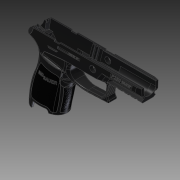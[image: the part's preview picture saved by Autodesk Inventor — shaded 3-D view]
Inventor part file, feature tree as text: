
AUTODESK INVENTOR PART (.ipt)
format: ipt  version: 2014 SP2 (Build 180246200, 246)  size: 58,253,824 bytes
history: native  units: in
note: dims shown in document units (in); Inventor stores cm internally (conversion verified against a paired STEP export)
features: sketch x143, projected_geometry x76, extrude x69, plane x53, reference x51, fillet x25, other x19, sweep x17, loft x7, delete_face x6, mirror x5, boolean_combine x5, surface_op x5, split x3, emboss x3, move_body x2, imported_body x1, chamfer x1, pattern_linear x1, revolve x1
ambient origin geometry x8: Origin, YZ Plane, XZ Plane, XY Plane, X Axis, Y Axis, Z Axis, Center Point
bodies: Solid6 (feature_tree), Solid9 (feature_tree), Solid23 (feature_tree), Solid7 (feature_tree), Solid8 (feature_tree), Solid10 (feature_tree), Solid21 (feature_tree), Solid22 (feature_tree)
feature tree (493):
  sketch  "Sketch1"  dims[d1=4.4533in d14=75.0deg]
  sketch  "Sketch2"  dims[d15=0.8575in d16=15.0deg]
  plane  "Work Plane1"
  plane  "Work Plane2"
  plane  "Work Plane6"
  plane  "Work Plane21"
  sketch  "Sketch12"  dims[d17=0.045in d18=4.1515in]
  plane  "Work Plane22"
  plane  "Work Plane29"
  sketch  "Sketch47"  dims[d19=90.0deg d20=90.0deg d21=0.5625in]
  sketch  "Sketch48"  dims[d22=0.5in d23=0.638in]
  plane  "Work Plane30"
  sketch  "Sketch49"  dims[d24=2.26in d25=0.6031in]
  plane  "Work Plane32"
  plane  "Work Plane31"
  loft  "Loft14"
  extrude  "Extrusion11"  TaperAngle=15.0deg  [1 undecoded]
  mirror  "Mirror2"
  sweep  "Sweep13"
  sketch  "Sketch65"  dims[d189=1.313in d190=0.5625in]
  sketch  "Sketch66"  dims[d191=0.0in d218=0.0in d219=90.0deg]
  sketch  "Sketch67"  dims[d220=0.0in d221=90.0deg d222=0.0in d223=90.0deg]
  sketch  "Sketch68"  dims[d224=0.0in d225=90.0deg d227=1.0in d228=0.0in]
  plane  "Work Plane34"
  loft  "Loft16"
  mirror  "Mirror4"
  sweep  "Sweep15"
  mirror  "Mirror5"
  sketch  "Sketch72"  dims[d255=0.0in d256=90.0deg d257=1.4375in]
  sketch  "Sketch73"  dims[d258=0.0in d264=0.149in]
  sketch  "Sketch74"  dims[d267=0.507in d268=1.2in]
  plane  "Work Plane35"
  sketch  "Sketch75"  dims[d275=0.7171in d276=0.0in d298=2.7754in d310=0.5065in]
  extrude  "Extrusion16"  Depth=0.6031in
  split  "Split1"
  boolean_combine  "Combine1"
  sketch  "Sketch104"  dims[d313=2.4322in d314=0.0in d315=90.0deg]
  sketch  "Sketch105"  dims[d316=0.0in d317=90.0deg d318=0.0in d319=90.0deg]
  loft  "Loft19"
  delete_face  "Delete Face1"
  delete_face  "Delete Face2"
  delete_face  "Delete Face3"
  delete_face  "Delete Face4"
  plane  "Work Plane37"
  plane  "Work Plane38"
  plane  "Work Plane39"
  plane  "Work Plane40"
  boolean_combine  "Combine3"
  fillet  "Fillet14"  Radius=0.3232in
  plane  "Work Plane41"
  extrude  "Extrusion18"  TaperAngle=0.0deg  [1 undecoded]
  sketch  "Sketch116"  dims[d363=0.005in d364=1.0in d365=0.0in]
  plane  "Work Plane42"
  extrude  "Extrusion19"  Depth=0.5625in
  extrude  "Extrusion20"  TaperAngle=0.0deg  [1 undecoded]
  sketch  "Sketch119"  dims[d371=0.005in d372=1.0in d373=0.0in]
  plane  "Work Plane43"
  plane  "Work Plane44"
  extrude  "Extrusion21"  TaperAngle=0.0deg  [1 undecoded]
  sweep  "Sweep20"
  extrude  "Extrusion22"  TaperAngle=0.0deg  [1 undecoded]
  plane  "Work Plane45"
  extrude  "Extrusion23"  TaperAngle=0.0deg  [1 undecoded]
  extrude  "Extrusion24"  TaperAngle=0.0deg  [1 undecoded]
  extrude  "Extrusion25"  Depth=1.4375in
  plane  "Work Plane46"
  sweep  "Sweep21"
  extrude  "Extrusion26"  Depth=1.2in
  extrude  "Extrusion27"  Depth=2.7754in
  fillet  "Fillet18"  Radius=0.5065in
  imported_body  "Base1"
  move_body  "Move Body1"
  extrude  "Extrusion28"  Depth=2.4322in
  move_body  "Move Body2"
  extrude  "Extrusion29"  TaperAngle=0.0deg  [1 undecoded]
  extrude  "Extrusion30"  TaperAngle=0.0deg  [1 undecoded]
  extrude  "Extrusion33"  Depth=0.005in
  extrude  "Extrusion34"  Depth=1.0in TaperAngle=0.0deg
  sketch  "Sketch138"  dims[d412=0.303in]
  extrude  "Extrusion35"  TaperAngle=90.0deg  [1 undecoded]
  extrude  "Extrusion36"  Depth=1.0in TaperAngle=0.0deg
  sweep  "Sweep23"
  extrude  "Extrusion37"  Depth=0.005in
  chamfer  "Chamfer1"  Distance=1.0in
  plane  "Work Plane51"
  extrude  "Extrusion44"  Depth=0.762in
  sketch  "Sketch144"  dims[d417=0.05in d418=0.0in d419=0.0in]
  plane  "Work Plane53"
  extrude  "Extrusion45"  Depth=0.6475in
  plane  "Work Plane54"
  extrude  "Extrusion46"  Depth=1.567in
  plane  "Work Plane55"
  extrude  "Extrusion47"  Depth=0.01in
  sweep  "Sweep26"
  sweep  "Sweep27"
  plane  "Work Plane56"
  extrude  "Extrusion52"  Depth=0.1945in
  fillet  "Fillet19"  Radius=3.5375in
  extrude  "Extrusion53"  Depth=3.5375in TaperAngle=0.0deg
  extrude  "Extrusion54"  TaperAngle=0.0deg  [1 undecoded]
  pattern_linear  "Rectangular Pattern1"  Count1=4 Spacing1=0.3937in
  sketch  "Sketch166"  dims[d445=0.138in]
  extrude  "Extrusion55"  Depth=1.2795in
  extrude  "Extrusion56"  Depth=0.0098in TaperAngle=0.0deg
  sketch  "Sketch167"  dims[d446=0.2135in]
  plane  "Work Plane57"
  sketch  "Sketch168"  dims[d447=0.679in]
  plane  "Work Plane58"
  extrude  "Extrusion57"  Depth=0.4764in
  extrude  "Extrusion58"  Depth=0.5602in
  extrude  "Extrusion59"  Depth=0.0134in TaperAngle=0.0deg
  sweep  "Sweep28"
  plane  "Work Plane59"
  extrude  "Extrusion60"  Depth=0.0134in TaperAngle=0.0deg
  sketch  "Sketch174"  dims[d457=0.013in d458=0.0in]
  sketch  "Sketch175"  dims[d459=0.0in]
  extrude  "Extrusion61"  [1 undecoded]
  extrude  "Extrusion62"  Depth=0.2295in
  extrude  "Extrusion63"  Depth=0.089in
  plane  "Work Plane73"
  sweep  "Sweep29"
  plane  "Work Plane60"
  extrude  "Extrusion64"  Depth=3.0134in TaperAngle=0.0deg
  fillet  "Fillet21"  Radius=0.0787in
  extrude  "Extrusion65"  TaperAngle=0.0deg  [1 undecoded]
  extrude  "Extrusion66"  Depth=0.1969in
  sweep  "Sweep30"
  fillet  "Fillet22"  Radius=0.3884in
  fillet  "Fillet23"  Radius=0.05in
  sketch  "Sketch186"  dims[d477=0.1079in]
  extrude  "Extrusion70"  Depth=0.01in TaperAngle=0.0deg
  fillet  "Fillet24"  [1 undecoded]
  other  "OUTLINE"
  plane  "Work Plane62"
  sketch  "Sketch197"  dims[d488=0.8325in]
  extrude  "Extrusion72"  Depth=0.025in
  boolean_combine  "Combine4"
  extrude  "Extrusion73"  Depth=0.09in
  extrude  "Extrusion74"  Depth=0.075in
  extrude  "Extrusion75"  Depth=0.8765in TaperAngle=0.0deg
  extrude  "Extrusion76"  Depth=0.8765in TaperAngle=0.0deg
  fillet  "Fillet27"  Radius=0.8765in
  extrude  "Extrusion77"  Depth=0.15in
  sketch  "Sketch219"  dims[d512=0.3779in]
  plane  "Work Plane65"
  extrude  "Extrusion78"  TaperAngle=0.0deg  [1 undecoded]
  plane  "Work Plane66"
  plane  "Work Plane70"
  sketch  "Sketch226"  dims[d513=0.2425in]
  plane  "Work Plane71"
  extrude  "Extrusion80"  Depth=0.125in
  sweep  "Sweep33"
  plane  "Work Plane72"
  sketch  "Sketch233"  dims[d518=0.0in]
  sketch  "Sketch234"  dims[d527=0.125in]
  split  "Split7"
  loft  "Loft27"
  boolean_combine  "Combine5"
  extrude  "Extrusion84"  Depth=1.0321in
  sketch  "Sketch237"  dims[d531=0.2106in]
  sketch  "Sketch238"  dims[d532=0.1685in]
  sweep  "Sweep34"
  plane  "Work Plane75"
  surface_op  "Trim1"
  surface_op  "Trim2"
  sketch  "Sketch261"  dims[d543=0.4945in d544=0.0098in d545=0.0in]
  surface_op  "Stitch Surface2"
  boolean_combine  "Combine6"
  plane  "Work Plane76"
  sketch  "Sketch262"  dims[d546=0.0098in d547=0.0in d548=0.4764in]
  plane  "Work Plane77"
  extrude  "Extrusion90"  Depth=0.5822in
  fillet  "Fillet41"  Radius=2.1701in
  revolve  "Revolution1"  [1 undecoded]
  plane  "Work Plane78"
  extrude  "Extrusion91"  TaperAngle=0.0deg  [1 undecoded]
  split  "Split8"
  delete_face  "Delete Face7"
  surface_op  "Stitch Surface3"
  plane  "Work Plane79"
  plane  "Work Plane80"
  extrude  "Extrusion92"  Depth=1.0in TaperAngle=0.0deg
  delete_face  "Delete Face9"
  fillet  "Fillet48"  [1 undecoded]
  fillet  "Fillet49"  [1 undecoded]
  fillet  "Fillet50"  [1 undecoded]
  fillet  "Fillet51"  Radius=0.375in
  fillet  "Fillet52"  Radius=0.375in
  fillet  "Fillet53"  [1 undecoded]
  fillet  "Fillet54"  [1 undecoded]
  fillet  "Fillet55"  [1 undecoded]
  extrude  "Extrusion93"  TaperAngle=0.0deg  [1 undecoded]
  extrude  "Extrusion94"  TaperAngle=0.0deg  [1 undecoded]
  fillet  "Fillet58"  [1 undecoded]
  fillet  "Fillet59"  Radius=1.0in
  extrude  "Extrusion95"  Depth=0.0137in
  extrude  "Extrusion96"  [1 undecoded]
  extrude  "Extrusion97"  Depth=0.25in TaperAngle=0.0deg
  sweep  "Sweep35"
  extrude  "Extrusion98"  Depth=0.1969in
  mirror  "Mirror12"
  extrude  "Extrusion99"  Depth=0.1969in
  extrude  "Extrusion100"  Depth=0.1969in
  extrude  "Extrusion101"  Depth=0.1969in
  extrude  "Extrusion102"  Depth=0.1969in
  extrude  "Extrusion103"  Depth=0.1969in
  fillet  "Fillet60"  Radius=0.1969in
  sweep  "Sweep36"
  sketch  "Sketch298"  dims[d643=1.0in d644=0.0in d645=0.0in]
  plane  "Work Plane83"
  extrude  "Extrusion104"  Depth=0.1969in
  sketch  "Sketch299"  dims[d646=1.0in d647=0.0in d648=0.125in]
  plane  "Work Plane84"
  extrude  "Extrusion105"  TaperAngle=0.0deg  [1 undecoded]
  fillet  "Fillet61"  [1 undecoded]
  fillet  "Fillet62"  Radius=1.0in
  fillet  "Fillet63"  Radius=0.0369in
  fillet  "Fillet64"  Radius=0.4in
  plane  "Work Plane85"
  sketch  "Sketch300"  dims[d671=0.765in d672=90.0deg]
  sketch  "3D Sketch50"
  plane  "Work Plane86"
  sweep  "Sweep37"
  mirror  "Mirror13"
  plane  "Work Plane87"
  sketch  "Sketch302"  dims[d682=90.0deg d683=1.0321in]
  sketch  "3D Sketch51"
  plane  "Work Plane88"
  sweep  "Sweep38"
  plane  "Work Plane89"
  sketch  "Sketch305"  dims[d686=2.1701in d688=0.5822in d689=2.1701in]
  sketch  "3D Sketch52"
  plane  "Work Plane90"
  sweep  "Sweep40"
  plane  "Work Plane91"
  emboss  "Emboss2"
  plane  "Work Plane92"
  emboss  "Emboss3"
  extrude  "Extrusion106"  Depth=1.5in
  other  "Move Face2"
  emboss  "Emboss4"
  extrude  "Extrusion107"  Depth=0.04in
  fillet  "Fillet65"  Radius=0.02in
  other  "Image1"
  reference  "Reference1"
  reference  "Reference2"
  reference  "Reference3"
  reference  "Reference4"
  reference  "Reference5"
  reference  "Reference6"
  reference  "Reference7"
  reference  "Reference8"
  reference  "Reference9"
  reference  "Reference10"
  sketch  "Sketch62"  dims[d51=1.056in d53=0.6395in d55=0.3232in]
  projected_geometry  "Projected Loop23"
  sketch  "Sketch63"  dims[d56=0.3593in d187=0.0in]
  projected_geometry  "Projected Loop25"
  projected_geometry  "Projected Loop26"
  sketch  "Sketch69"  dims[d243=0.5822in d245=0.0in]
  other  "Edges3"
  sketch  "Sketch70"  dims[d247=0.0in d248=90.0deg d249=0.0in d250=90.0deg]
  projected_geometry  "Projected Loop27"
  sketch  "Sketch71"  dims[d251=0.0in d252=90.0deg d253=0.0in d254=90.0deg]
  sketch  "Sketch101"  dims[d311=0.5065in d312=2.4322in]
  projected_geometry  "Projected Loop34"
  sketch  "3D Sketch23"
  sketch  "Sketch115"  dims[d336=0.3125in d362=0.005in]
  reference  "Reference11"
  reference  "Reference12"
  reference  "Reference13"
  reference  "Reference14"
  reference  "Reference15"
  reference  "Reference16"
  reference  "Reference17"
  reference  "Reference18"
  reference  "Reference19"
  sketch  "Sketch117"  dims[d366=0.01in d367=90.0deg]
  reference  "Reference20"
  reference  "Reference21"
  sketch  "Sketch118"  dims[d368=0.01in d369=1.0in d370=0.0in]
  reference  "Reference22"
  reference  "Reference23"
  reference  "Reference24"
  reference  "Reference25"
  reference  "Reference26"
  reference  "Reference27"
  reference  "Reference28"
  reference  "Reference29"
  reference  "Reference30"
  reference  "Reference31"
  sketch  "Sketch120"  dims[d374=0.01in d375=0.005in]
  projected_geometry  "Projected Loop37"
  sketch  "Sketch121"  dims[d378=0.01in]
  projected_geometry  "Projected Loop38"
  sketch  "3D Sketch27"
  sketch  "Sketch122"  dims[d379=-0.0745in]
  projected_geometry  "Projected Loop39"
  projected_geometry  "Projected Loop40"
  reference  "Reference32"
  reference  "Reference33"
  reference  "Reference34"
  reference  "Reference35"
  reference  "Reference36"
  sketch  "Sketch123"  dims[d380=0.025in]
  reference  "Reference37"
  sketch  "Sketch125"  dims[d381=0.2188in d382=1.0in d383=0.0in]
  projected_geometry  "Projected Loop42"
  sketch  "Sketch126"  dims[d384=0.0in d385=0.762in]
  reference  "Reference38"
  sketch  "Sketch127"  dims[d386=0.1455in d388=0.6475in]
  sketch  "Sketch128"  dims[d389=0.01in d390=1.567in]
  sketch  "Sketch129"  dims[d391=0.68in d392=0.01in]
  sketch  "Sketch130"  dims[d393=0.01in d394=1.0in d395=0.0in]
  projected_geometry  "Projected Loop43"
  sketch  "Sketch131"  dims[d396=0.19in d397=0.01in]
  sketch  "Sketch132"  dims[d398=0.085in d399=0.0in d400=0.1945in d401=3.5375in d402=0.0in]
  reference  "Reference39"
  sketch  "Sketch133"  dims[d403=0.344in d404=3.5375in d405=0.0in]
  projected_geometry  "Projected Loop44"
  sketch  "Sketch136"  dims[d407=-0.286in d409=0.0in]
  reference  "Reference40"
  sketch  "Sketch137"  dims[d410=0.0in d411=0.0in]
  projected_geometry  "Projected Loop45"
  projected_geometry  "Projected Loop46"
  sketch  "Sketch139"  dims[d413=0.0785in]
  projected_geometry  "Projected Loop47"
  sketch  "Sketch140"  dims[d414=3.5375in d415=0.0in]
  projected_geometry  "Projected Loop48"
  sketch  "3D Sketch29"
  sketch  "Sketch141"  dims[d416=0.4in]
  projected_geometry  "Projected Loop49"
  projected_geometry  "Projected Loop52"
  sketch  "Sketch153"  dims[d421=0.3575in]
  projected_geometry  "Projected Loop58"
  sketch  "Sketch154"  dims[d422=3.5375in d423=0.0in]
  sketch  "Sketch155"  dims[d424=0.2645in]
  projected_geometry  "Projected Loop59"
  sketch  "Sketch156"  dims[d425=45.0deg]
  sketch  "Sketch157"  dims[d426=0.0in d427=0.015in d428=0.0in d429=0.02in]
  projected_geometry  "Projected Loop60"
  sketch  "Sketch158"  dims[d430=0.092in]
  projected_geometry  "Projected Loop61"
  sketch  "Sketch160"  dims[d431=0.6in]
  sketch  "Sketch164"  dims[d432=0.062in d433=0.0in]
  projected_geometry  "Projected Loop63"
  projected_geometry  "Projected Loop64"
  sketch  "Sketch165"  dims[d434=0.062in d435=0.0in]
  projected_geometry  "Projected Loop65"
  projected_geometry  "Projected Loop66"
  projected_geometry  "Projected Loop67"
  sketch  "Sketch169"  dims[d448=0.187in d449=0.0in]
  sketch  "Sketch170"  dims[d450=0.7in]
  projected_geometry  "Projected Loop68"
  sketch  "Sketch171"  dims[d451=0.013in d452=0.0in]
  projected_geometry  "Projected Loop69"
  sketch  "Sketch172"  dims[d454=0.6385in]
  projected_geometry  "Projected Loop70"
  projected_geometry  "Projected Loop71"
  sketch  "3D Sketch30"
  sketch  "Sketch173"  dims[d455=0.013in d456=0.0in]
  sketch  "Sketch176"  dims[d460=0.1718in]
  projected_geometry  "Projected Loop72"
  sketch  "Sketch177"  dims[d461=0.131in]
  projected_geometry  "Projected Loop73"
  sketch  "Sketch178"  dims[d462=0.1945in d463=0.0in]
  projected_geometry  "Projected Loop74"
  projected_geometry  "Projected Loop75"
  sketch  "Sketch179"  dims[d464=0.0625in d465=0.125in d466=45.0deg]
  projected_geometry  "Projected Loop76"
  sketch  "Sketch180"  dims[d467=-0.409in]
  sketch  "Sketch181"  dims[d472=90.0deg]
  projected_geometry  "Projected Loop77"
  sketch  "Sketch182"  dims[d474=0.6142in]
  sketch  "Sketch183"  dims[d475=0.3701in]
  projected_geometry  "Projected Loop78"
  sketch  "Sketch184"  dims[d476=0.748in]
  projected_geometry  "Projected Loop79"
  sketch  "3D Sketch31"
  projected_geometry  "Projected Loop81"
  projected_geometry  "Projected Loop82"
  sketch  "Sketch188"  dims[d478=0.1642in]
  projected_geometry  "Projected Loop83"
  projected_geometry  "Projected Loop86"
  sketch  "Sketch204"  dims[d489=0.3642in]
  projected_geometry  "Projected Loop87"
  sketch  "Sketch207"  dims[d502=0.1945in d503=0.0in]
  projected_geometry  "Projected Loop88"
  sketch  "Sketch208"  dims[d504=0.5695in d505=0.097in d506=0.0in d507=0.0in]
  sketch  "Sketch209"  dims[d508=0.257in d509=0.0in]
  sketch  "Sketch210"  dims[d510=0.1945in d511=0.0in]
  projected_geometry  "Projected Loop89"
  sketch  "Sketch228"  dims[d514=0.3642in]
  projected_geometry  "Projected Loop93"
  sketch  "Sketch229"  dims[d515=0.0in]
  sketch  "Sketch235"  dims[d528=0.1945in d529=0.0in]
  sketch  "Sketch236"  dims[d530=0.02in]
  projected_geometry  "Projected Loop95"
  projected_geometry  "Projected Loop96"
  sketch  "3D Sketch39"
  sketch  "Sketch257"  dims[d533=0.1945in d534=0.0in]
  other  "Srf15"
  sketch  "Sketch258"  dims[d535=0.7945in]
  other  "Srf16"
  sketch  "Sketch259"  dims[d536=0.1945in d537=0.0in d538=1.5748in d540=0.3937in]
  sketch  "Sketch260"  dims[d541=0.2165in d542=1.2795in]
  other  "Edges8"
  other  "Edges9"
  other  "Srf17"
  other  "Edges10"
  other  "Edges11"
  other  "Edges12"
  other  "Edges13"
  other  "Srf18"
  sketch  "Sketch268"  dims[d549=90.0deg d550=0.5602in]
  projected_geometry  "Projected Loop100"
  sketch  "Sketch272"  dims[d551=0.5602in d552=0.0134in d553=0.0in]
  sketch  "Sketch273"  dims[d554=0.0134in d555=0.0in d556=0.1283in]
  sketch  "Sketch274"  dims[d557=0.5497in d558=0.0134in d559=0.0in]
  projected_geometry  "Projected Loop102"
  other  "Srf19"
  sketch  "Sketch276"  dims[d560=0.0in d561=-0.3197in]
  sketch  "Sketch279"  dims[d562=0.6429in d563=0.2295in]
  sketch  "Sketch283"  dims[d564=0.0134in d565=0.0in d566=0.089in]
  sketch  "3D Sketch48"
  other  "Srf21"
  sketch  "Sketch284"  dims[d567=0.028in d568=3.0134in d569=0.0in]
  projected_geometry  "Projected Loop105"
  sketch  "Sketch285"  dims[d570=3.0134in d571=0.0in d572=3.0134in d573=0.0in d575=0.0787in]
  projected_geometry  "Projected Loop106"
  sketch  "Sketch286"  dims[d576=0.0787in d577=0.0in]
  projected_geometry  "Projected Loop107"
  sketch  "Sketch287"  dims[d578=-3.8125in d579=0.1969in]
  sketch  "Sketch288"  dims[d580=0.1299in d581=0.2264in d582=0.3884in d583=0.0in d584=0.05in]
  projected_geometry  "Projected Loop108"
  sketch  "Sketch289"  dims[d585=0.3884in d586=0.0in d587=0.01in d588=0.0in d589=0.0in]
  sketch  "Sketch291"  dims[d590=0.025in d591=0.025in]
  projected_geometry  "Projected Loop110"
  sketch  "Sketch292"  dims[d601=0.311in d602=0.0in d603=0.09in]
  sketch  "Sketch293"  dims[d608=0.7657in d609=0.075in]
  projected_geometry  "Projected Loop111"
  sketch  "Sketch294"  dims[d610=-0.6875in d618=0.8765in d619=0.0in]
  sketch  "Sketch295"  dims[d625=0.8765in d626=0.0in d627=0.8765in d628=0.0in d629=0.8765in d630=0.0in]
  sketch  "Sketch296"  dims[d631=0.8765in d632=0.0in]
  sketch  "Sketch297"  dims[d634=0.05in d635=0.63in d636=0.05in d637=0.3937in d638=0.5in d639=0.0in d640=0.15in d641=0.1969in]
  projected_geometry  "Projected Loop112"
  sketch  "3D Sketch49"
  projected_geometry  "Projected Loop113"
  sketch  "Sketch301"  dims[d673=1.3125in d674=0.0in d677=0.0in]
  sketch  "Sketch303"  dims[d684=0.0448in d685=0.5822in]
  sketch  "Sketch306"  dims[d690=2.4322in d691=0.5065in]
  sketch  "Sketch307"  dims[d692=0.0448in d693=0.0in d694=90.0deg]
  sketch  "Sketch308"  dims[d695=0.0in d696=90.0deg d697=1.0in d698=0.0in d699=0.0in d700=0.0in d764=-0.0339in d766=0.375in d767=0.0in d768=0.375in d769=0.0in d770=0.0in d771=90.0deg d772=0.0in d773=90.0deg d774=0.0in d775=90.0deg]
  sketch  "Sketch309"  dims[d776=0.0in d777=90.0deg d778=0.0in d779=90.0deg]
  reference  "Reference41"
  reference  "Reference42"
  reference  "Reference43"
  reference  "Reference44"
  reference  "Reference45"
  reference  "Reference46"
  reference  "Reference47"
  reference  "Reference48"
  reference  "Reference49"
  reference  "Reference50"
  reference  "Reference51"
  sketch  "Sketch310"  dims[d780=0.0in d781=90.0deg d782=0.0in d783=90.0deg d784=0.0in d785=90.0deg d801=1.0in d802=0.0in]
  sketch  "Sketch312"  dims[d811=0.08in d812=0.1in d813=0.05in d814=0.0812in d815=0.19in d816=0.3937in d817=0.2in d818=0.3937in d819=0.08in d820=0.0in d821=0.15in d822=0.1969in d823=0.05in d824=0.3937in d825=0.0137in d826=-1.1875in d827=0.25in d828=0.0in d829=0.1969in d830=0.1969in d831=0.1969in d832=0.1969in d833=0.1969in d834=0.1969in d835=0.1969in d836=0.1969in d837=0.1969in d838=0.1969in d839=0.0in d841=90.0deg d842=1.0in d843=0.0in d850=0.0369in d851=0.4in d852=0.5in d853=0.37in d854=0.08in d855=1.5in d856=0.04in d857=0.02in d864=0.26in d865=0.13in d866=0.0in d867=0.0in d877=0.0in d878=90.0deg d879=0.0in d880=90.0deg d881=0.26in d882=0.0in d883=0.02in d884=0.0498in d885=0.01in d886=0.0498in d887=0.01in d888=0.0in d889=0.26in d890=0.0in d891=75.0deg d892=0.26in d893=0.0in d894=75.0deg d895=0.005in d896=0.0in d897=0.258in d898=0.0in d899=0.005in d900=0.0in d901=0.005in d902=0.0in d903=0.005in d904=0.0in d905=0.052in d906=0.018in d907=0.0in d908=0.126in d909=0.134in d910=0.2886in d911=1.1681in d912=0.0815in d913=0.0in d914=0.01in d915=0.99in d916=0.446in d917=0.0in d918=0.1in d919=0.6475in d920=0.0in d921=0.0955in d922=0.0955in d923=0.2in d924=-0.074in d925=0.446in d926=0.0in d927=-0.0945in d928=0.446in d929=0.0in d930=0.04in d931=0.018in d932=0.018in d933=0.025in d934=0.8125in d935=0.375in d936=0.125in d938=0.1145in d939=0.115in d940=0.345in d941=5.0in d942=0.25in d943=0.125in d944=0.08in d945=0.0in d946=-3.75in d947=0.2495in d948=0.4in d949=0.093in d951=0.125in d952=0.08in d953=0.2489in d954=0.08in d956=0.0in d957=-0.75in d960=0.08in d961=0.125in d963=0.0in d964=0.375in d965=0.01in d966=0.0in d967=0.1875in d968=0.01in d969=0.0in d970=0.005in d971=0.446in d972=0.0in d975=0.043in d976=0.005in d977=0.0in d979=0.487in d980=0.446in d981=0.0in d982=0.011in]
  extrude  "ExtrusionSrf5"  Depth=0.26in TaperAngle=0.0deg
  extrude  "ExtrusionSrf6"  TaperAngle=0.0deg  [1 undecoded]
  loft  "LoftSrf2"
  loft  "LoftSrf5"
  projected_geometry  "Project Cut Edges13"
  projected_geometry  "Project Cut Edges14"
  projected_geometry  "Project Cut Edges15"
  projected_geometry  "Project Cut Edges32"
  projected_geometry  "Project Cut Edges38"
  projected_geometry  "Project Cut Edges40"
  projected_geometry  "Project Cut Edges42"
  projected_geometry  "Project Cut Edges43"
  projected_geometry  "Project Cut Edges44"
  projected_geometry  "Project Cut Edges45"
  projected_geometry  "Project Cut Edges56"
  loft  "LoftSrf3"
  projected_geometry  "Project Cut Edges60"
  projected_geometry  "Project Cut Edges62"
  surface_op  "Boundary Patch5"
  projected_geometry  "Project Cut Edges64"
  projected_geometry  "Project Cut Edges65"
  projected_geometry  "Project Cut Edges66"
  other  "3D Intersection8"
  other  "3D Intersection9"
  other  "3D Intersection10"
  projected_geometry  "Project Cut Edges68"
note: 30 required parameter values undecoded (feature->parameter linkage not recoverable at this tier; creation-order binding heuristic only, values carry confidence <= 0.55)